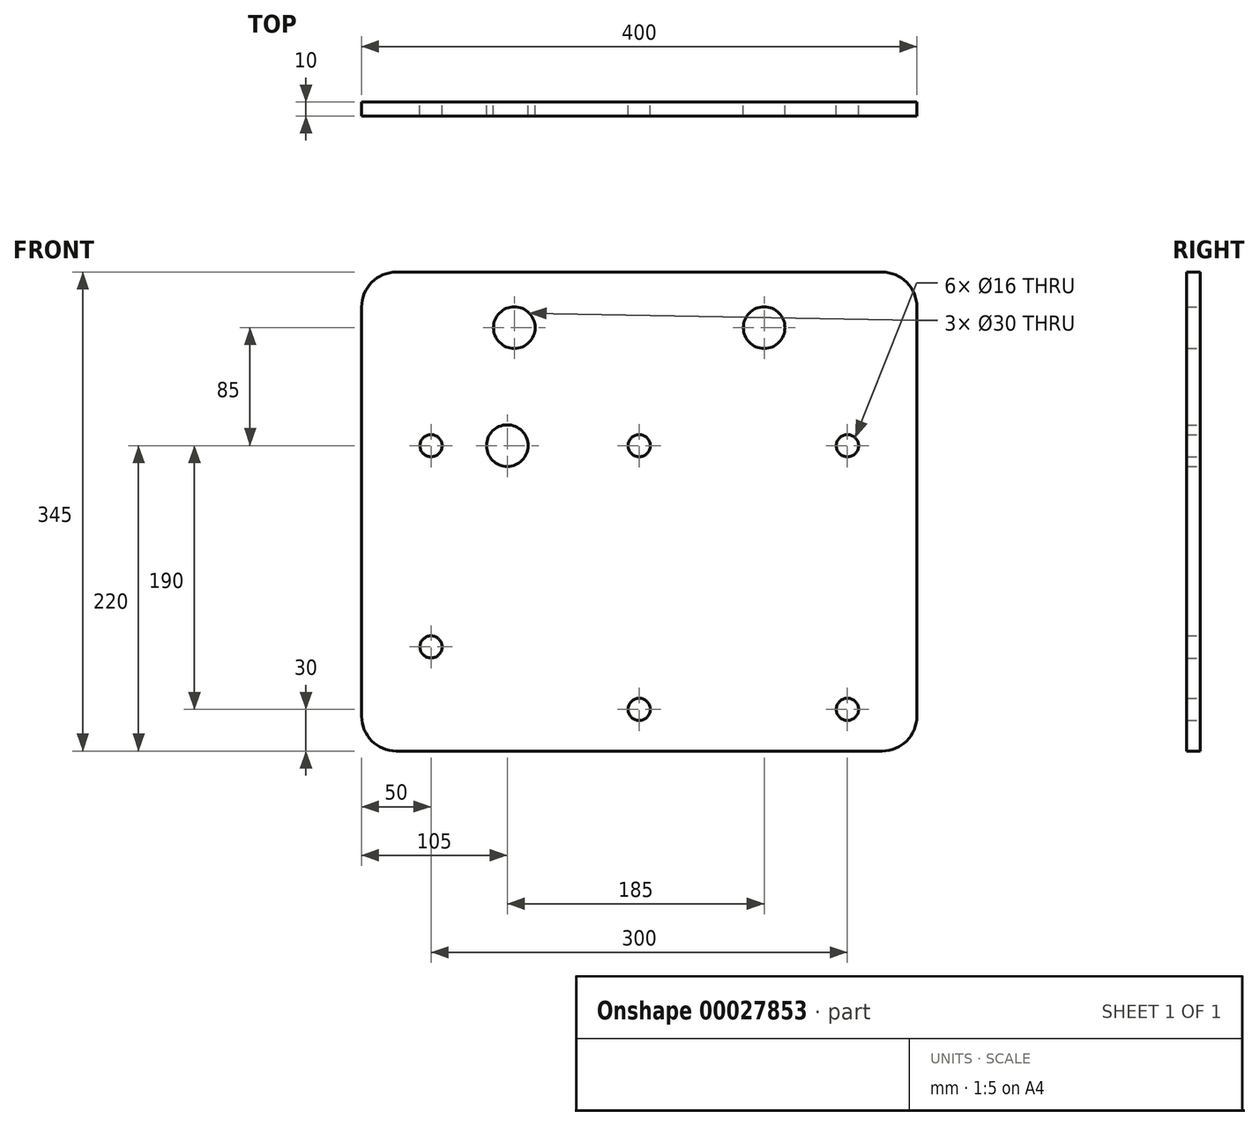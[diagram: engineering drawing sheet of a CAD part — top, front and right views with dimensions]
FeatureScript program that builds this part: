
annotation { "Feature Type Name" : "Feature", "Feature Type Description" : "" }
export const myFeature = defineFeature(function(context is Context, id is Id, definition is map)
    precondition{}
    {
        {
            var Q0;
            Q0=qCreatedBy(makeId("Front.planeOp"),FACE);
            var sketch = newSketch(context, id + "F0", { "sketchPlane" : qUnion([Q0])});
            skLineSegment(sketch, "E0.bottom", {"start": v(-25, 0) * mm, "end": v(-375, 0) * mm});
            skLineSegment(sketch, "E0.top", {"start": v(-25, 345) * mm, "end": v(-375, 345) * mm});
            skLineSegment(sketch, "E0.left", {"start": v(0, 25) * mm, "end": v(0, 320) * mm});
            skLineSegment(sketch, "E0.right", {"start": v(-400, 25) * mm, "end": v(-400, 320) * mm});
            skPoint(sketch, "E1.visualSharp", {"position": v(-400, 345) * mm});
            skArc(sketch, "E1.filletArc", {"start": v(-375, 345) * mm, "mid": v(-392.68, 337.68) * mm, "end": v(-400, 320) * mm});
            skPoint(sketch, "E2.visualSharp", {"position": v(0, 345) * mm});
            skArc(sketch, "E2.filletArc", {"start": v(0, 320) * mm, "mid": v(-7.32, 337.68) * mm, "end": v(-25, 345) * mm});
            skPoint(sketch, "E3.visualSharp", {"position": v(-400, 0) * mm});
            skArc(sketch, "E3.filletArc", {"start": v(-400, 25) * mm, "mid": v(-392.68, 7.32) * mm, "end": v(-375, 0) * mm});
            skPoint(sketch, "E4.visualSharp", {"position": v(0, 0) * mm});
            skArc(sketch, "E4.filletArc", {"start": v(-25, 0) * mm, "mid": v(-7.32, 7.32) * mm, "end": v(0, 25) * mm});
            skCircle(sketch, "E5", {"center": v(-290, 305) * mm, "radius": 15 * mm});
            skCircle(sketch, "E6", {"center": v(-110, 305) * mm, "radius": 15 * mm});
            skCircle(sketch, "E7", {"center": v(-350, 75) * mm, "radius": 8 * mm});
            skCircle(sketch, "E8", {"center": v(-350, 220) * mm, "radius": 8 * mm});
            skCircle(sketch, "E9", {"center": v(-295, 220) * mm, "radius": 15 * mm});
            skCircle(sketch, "E10", {"center": v(-200, 220) * mm, "radius": 8 * mm});
            skCircle(sketch, "E11", {"center": v(-50, 220) * mm, "radius": 8 * mm});
            skCircle(sketch, "E12", {"center": v(-200, 30) * mm, "radius": 8 * mm});
            skCircle(sketch, "E13", {"center": v(-50, 30) * mm, "radius": 8 * mm});
            skSolve(sketch);
        }
        {
            var Q0;
            Q0=makeQuery(id+"F0.imprint","IMPRINT",FACE,{"disambiguationData":[TD([[makeQuery(id+"F0.imprint","IMPRINT",EDGE,{"derivedFrom":sQuery(id+"F0.wireOp",EDGE,"E0.bottom")}),-1.0]])]});
            extrude(context, id + "F1", {"entities" : qUnion([Q0]), "depth" : 10 * mm});
        }
    });
